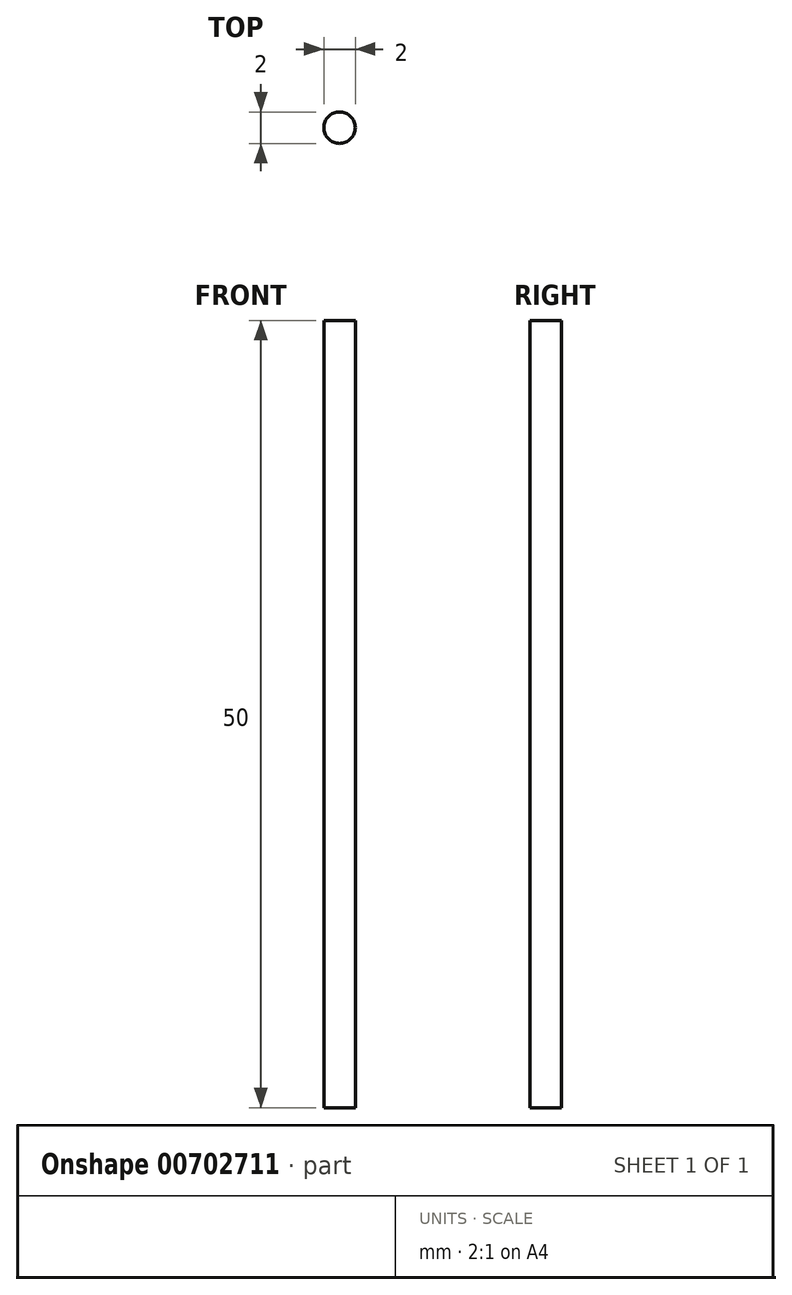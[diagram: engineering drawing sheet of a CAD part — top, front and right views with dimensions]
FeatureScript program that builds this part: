
annotation { "Feature Type Name" : "Feature", "Feature Type Description" : "" }
export const myFeature = defineFeature(function(context is Context, id is Id, definition is map)
    precondition{}
    {
        {
            var Q0;
            Q0=qCreatedBy(makeId("Top.planeOp"),FACE);
            var sketch = newSketch(context, id + "F0", { "sketchPlane" : qUnion([Q0])});
            skCircle(sketch, "E0", {"center": v(0, 0) * mm, "radius": 1 * mm});
            skSolve(sketch);
        }
        {
            var Q0;
            Q0=makeQuery(id+"F0.imprint","IMPRINT",FACE,{"disambiguationData":[TD([[makeQuery(id+"F0.imprint","IMPRINT",EDGE,{"derivedFrom":sQuery(id+"F0.wireOp",EDGE,"E0")}),1.0]])]});
            extrude(context, id + "F1", {"entities" : qUnion([Q0]), "depth" : 50 * mm, "offsetDistance" : 25.4 * mm});
        }
    });
